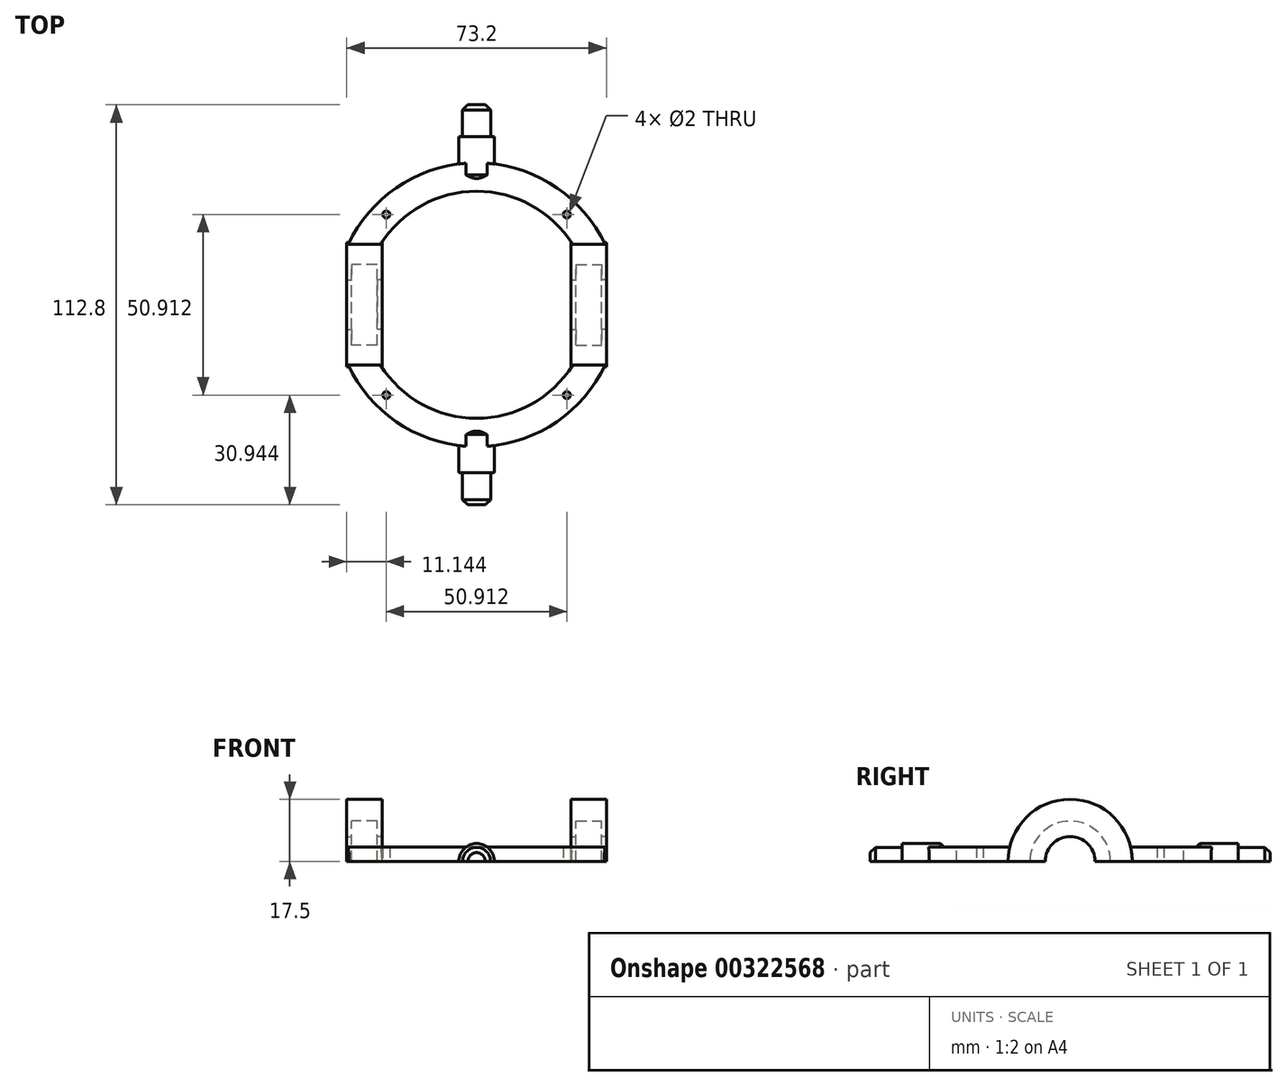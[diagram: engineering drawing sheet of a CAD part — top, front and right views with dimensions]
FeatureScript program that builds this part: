
annotation { "Feature Type Name" : "Feature", "Feature Type Description" : "" }
export const myFeature = defineFeature(function(context is Context, id is Id, definition is map)
    precondition{}
    {
        {
            var Q0;
            Q0=qCreatedBy(makeId("Top.planeOp"),FACE);
            var sketch = newSketch(context, id + "F0", { "sketchPlane" : qUnion([Q0])});
            skCircle(sketch, "E0", {"center": v(0, 0) * mm, "radius": 50 * mm});
            skCircle(sketch, "E1", {"center": v(0, 0) * mm, "radius": 58 * mm});
            skSolve(sketch);
        }
        {
            var Q0;
            Q0=qSketchRegion(id+"F0",true);
            extrude(context, id + "F1", {"entities" : qUnion([Q0]), "depth" : 4 * mm, "hasSecondDirection" : true, "secondDirectionOppositeDirection" : true, "secondDirectionDepth" : 4 * mm});
        }
        {
            var Q0;
            Q0=qCreatedBy(makeId("Front.planeOp"),FACE);
            cPlane(context, id + "F2", {"entities" : qUnion([Q0]), "cplaneType" : CPlaneType.OFFSET, "offset" : 54.8 * mm, "width" : 150 * mm, "height" : 150 * mm});
        }
        {
            var Q0;
            Q0=qCreatedBy(id+"F2.planeOp",FACE);
            var sketch = newSketch(context, id + "F3", { "sketchPlane" : qUnion([Q0])});
            skCircle(sketch, "E2", {"center": v(0, 0) * mm, "radius": 11.35 * mm});
            skCircle(sketch, "E3", {"center": v(0, 0) * mm, "radius": 17.5 * mm});
            skSolve(sketch);
        }
        {
            var Q0;
            Q0=makeQuery(id+"F3.imprint","IMPRINT",FACE,{"disambiguationData":[TD([[makeQuery(id+"F3.imprint","IMPRINT",EDGE,{"derivedFrom":sQuery(id+"F3.wireOp",EDGE,"E2")}),1.0]])]});
            var Q1;
            Q1=makeQuery(id+"F3.imprint","IMPRINT",FACE,{"disambiguationData":[TD([[makeQuery(id+"F3.imprint","IMPRINT",EDGE,{"derivedFrom":sQuery(id+"F3.wireOp",EDGE,"E2")}),-1.0]])]});
            extrude(context, id + "F4", {"entities" : qUnion([Q0, Q1]), "operationType" : NewBodyOperationType.REMOVE, "oppositeDirection" : true, "depth" : 25 * mm, "hasSecondDirection" : true, "secondDirectionOppositeDirection" : false, "secondDirectionDepth" : 25 * mm});
        }
        {
            var Q0;
            Q0=makeQuery(id+"F3.imprint","IMPRINT",FACE,{"disambiguationData":[TD([[makeQuery(id+"F3.imprint","IMPRINT",EDGE,{"derivedFrom":sQuery(id+"F3.wireOp",EDGE,"E2")}),-1.0]])]});
            extrude(context, id + "F5", {"entities" : qUnion([Q0]), "operationType" : NewBodyOperationType.ADD, "oppositeDirection" : true, "depth" : 7.2 * mm});
        }
        {
            var Q0;
            Q0=makeQuery(id+"F5.opExtrude","CAP_FACE",FACE,{"disambiguationData":[OSD([sQuery(id+"F3.wireOp",EDGE,"E2"),sQuery(id+"F3.wireOp",EDGE,"E3")])],"isStart":true});
            var sketch = newSketch(context, id + "F6", { "sketchPlane" : qUnion([Q0])});
            skCircle(sketch, "E4", {"center": v(0, 0) * mm, "radius": 7 * mm});
            skCircle(sketch, "E5", {"center": v(0, 0) * mm, "radius": 17.5 * mm});
            skSolve(sketch);
        }
        {
            var Q0;
            Q0=makeQuery(id+"F6.imprint","IMPRINT",FACE,{"disambiguationData":[TD([[makeQuery(id+"F6.imprint","IMPRINT",EDGE,{"derivedFrom":sQuery(id+"F6.wireOp",EDGE,"E4")}),-1.0]])]});
            var Q1;
            Q1=makeQuery(id+"F6.imprint","IMPRINT",FACE,{"disambiguationData":[TD([[makeQuery(id+"F6.imprint","IMPRINT",EDGE,{"derivedFrom":sQuery(id+"F6.wireOp",EDGE,"E5")}),1.0]])]});
            extrude(context, id + "F7", {"entities" : qUnion([Q0, Q1]), "operationType" : NewBodyOperationType.ADD, "depth" : 1.4 * mm});
        }
        {
            var Q0;
            Q0=makeQuery(id+"F5.opExtrude","CAP_FACE",FACE,{"disambiguationData":[OSD([sQuery(id+"F3.wireOp",EDGE,"E2"),sQuery(id+"F3.wireOp",EDGE,"E3")])],"isStart":false});
            var sketch = newSketch(context, id + "F8", { "sketchPlane" : qUnion([Q0])});
            skCircle(sketch, "E6", {"center": v(0, 0) * mm, "radius": 7 * mm});
            skCircle(sketch, "E7", {"center": v(0, 0) * mm, "radius": 17.5 * mm});
            skSolve(sketch);
        }
        {
            var Q0;
            Q0=makeQuery(id+"F8.imprint","IMPRINT",FACE,{"disambiguationData":[TD([[makeQuery(id+"F8.imprint","IMPRINT",EDGE,{"derivedFrom":sQuery(id+"F8.wireOp",EDGE,"E7")}),-1.0]])]});
            var Q1;
            Q1=makeQuery(id+"F8.imprint","IMPRINT",FACE,{"disambiguationData":[TD([[makeQuery(id+"F8.imprint","IMPRINT",EDGE,{"derivedFrom":sQuery(id+"F8.wireOp",EDGE,"E6")}),-1.0]])]});
            extrude(context, id + "F9", {"entities" : qUnion([Q0, Q1]), "operationType" : NewBodyOperationType.ADD, "depth" : 1.4 * mm});
        }
        {
            var Q0;
            Q0=qCreatedBy(makeId("Front.planeOp"),FACE);
            cPlane(context, id + "F10", {"entities" : qUnion([Q0]), "cplaneType" : CPlaneType.OFFSET, "offset" : 54.8 * mm, "oppositeDirection" : true, "width" : 150 * mm, "height" : 150 * mm});
        }
        {
            var Q0;
            Q0=qCreatedBy(id+"F10.planeOp",FACE);
            var sketch = newSketch(context, id + "F11", { "sketchPlane" : qUnion([Q0])});
            skCircle(sketch, "E8", {"center": v(0, 0) * mm, "radius": 17.5 * mm});
            skCircle(sketch, "E9", {"center": v(0, 0) * mm, "radius": 11.35 * mm});
            skSolve(sketch);
        }
        {
            var Q0;
            Q0=makeQuery(id+"F11.imprint","IMPRINT",FACE,{"disambiguationData":[TD([[makeQuery(id+"F11.imprint","IMPRINT",EDGE,{"derivedFrom":sQuery(id+"F11.wireOp",EDGE,"E8")}),1.0]])]});
            var Q1;
            Q1=makeQuery(id+"F11.imprint","IMPRINT",FACE,{"disambiguationData":[TD([[makeQuery(id+"F11.imprint","IMPRINT",EDGE,{"derivedFrom":sQuery(id+"F11.wireOp",EDGE,"E9")}),1.0]])]});
            extrude(context, id + "F12", {"entities" : qUnion([Q0, Q1]), "operationType" : NewBodyOperationType.REMOVE, "depth" : 25 * mm, "hasSecondDirection" : true, "secondDirectionOppositeDirection" : true, "secondDirectionDepth" : 25 * mm});
        }
        {
            var Q0;
            Q0=makeQuery(id+"F11.imprint","IMPRINT",FACE,{"disambiguationData":[TD([[makeQuery(id+"F11.imprint","IMPRINT",EDGE,{"derivedFrom":sQuery(id+"F11.wireOp",EDGE,"E8")}),1.0]])]});
            extrude(context, id + "F13", {"entities" : qUnion([Q0]), "operationType" : NewBodyOperationType.ADD, "depth" : 7.2 * mm});
        }
        {
            var Q0;
            Q0=makeQuery(id+"F13.opExtrude","CAP_FACE",FACE,{"disambiguationData":[OSD([sQuery(id+"F11.wireOp",EDGE,"E8"),sQuery(id+"F11.wireOp",EDGE,"E9")])],"isStart":true});
            var sketch = newSketch(context, id + "F14", { "sketchPlane" : qUnion([Q0])});
            skCircle(sketch, "E10", {"center": v(0, 0) * mm, "radius": 7 * mm});
            skCircle(sketch, "E11", {"center": v(0, 0) * mm, "radius": 17.5 * mm});
            skSolve(sketch);
        }
        {
            var Q0;
            Q0=makeQuery(id+"F14.imprint","IMPRINT",FACE,{"disambiguationData":[TD([[makeQuery(id+"F14.imprint","IMPRINT",EDGE,{"derivedFrom":makeQuery(id+"F13.opExtrude","CAP_EDGE",EDGE,{"disambiguationData":[OSD([sQuery(id+"F11.wireOp",EDGE,"E9")])],"isStart":true})}),1.0]])]});
            var Q1;
            Q1=makeQuery(id+"F14.imprint","IMPRINT",FACE,{"disambiguationData":[TD([[makeQuery(id+"F14.imprint","IMPRINT",EDGE,{"derivedFrom":sQuery(id+"F14.wireOp",EDGE,"E10")}),-1.0]])]});
            extrude(context, id + "F15", {"entities" : qUnion([Q0, Q1]), "operationType" : NewBodyOperationType.ADD, "depth" : 1.4 * mm});
        }
        {
            var Q0;
            Q0=makeQuery(id+"F13.opExtrude","CAP_FACE",FACE,{"disambiguationData":[OSD([sQuery(id+"F11.wireOp",EDGE,"E8"),sQuery(id+"F11.wireOp",EDGE,"E9")])],"isStart":false});
            var sketch = newSketch(context, id + "F16", { "sketchPlane" : qUnion([Q0])});
            skCircle(sketch, "E12", {"center": v(0, 0) * mm, "radius": 7 * mm});
            skCircle(sketch, "E13", {"center": v(0, 0) * mm, "radius": 17.5 * mm});
            skSolve(sketch);
        }
        {
            var Q0;
            Q0=makeQuery(id+"F16.imprint","IMPRINT",FACE,{"disambiguationData":[TD([[makeQuery(id+"F16.imprint","IMPRINT",EDGE,{"derivedFrom":sQuery(id+"F16.wireOp",EDGE,"E12")}),-1.0]])]});
            var Q1;
            Q1=makeQuery(id+"F16.imprint","IMPRINT",FACE,{"disambiguationData":[TD([[makeQuery(id+"F16.imprint","IMPRINT",EDGE,{"derivedFrom":sQuery(id+"F16.wireOp",EDGE,"E13")}),1.0]])]});
            extrude(context, id + "F17", {"entities" : qUnion([Q0, Q1]), "operationType" : NewBodyOperationType.ADD, "depth" : 1.4 * mm});
        }
        {
            var Q0;
            Q0=makeQuery(id+"F12.boolean.opBoolean","SPLIT",FACE,{"disambiguationData":[OD(0.0)],"derivedFrom":makeQuery(id+"F1.opExtrude","CAP_FACE",FACE,{"disambiguationData":[OSD([sQuery(id+"F0.wireOp",EDGE,"E0"),sQuery(id+"F0.wireOp",EDGE,"E1")])],"isStart":false})});
            var sketch = newSketch(context, id + "F18", { "sketchPlane" : qUnion([Q0])});
            skLineSegment(sketch, "E14", {"start": v(0, 0) * mm, "end": v(-50, 0) * mm, "construction": true});
            skLineSegment(sketch, "E15", {"start": v(-50, 0) * mm, "end": v(-58, 0) * mm, "construction": true});
            skCircle(sketch, "E16", {"center": v(-54, 0) * mm, "radius": 3 * mm});
            skCircle(sketch, "E17", {"center": v(-54, 0) * mm, "radius": 1.5 * mm});
            skCircle(sketch, "E18", {"center": v(-54, 0) * mm, "radius": 1 * mm});
            skCircle(sketch, "E19.1.0", {"center": v(-27, -46.77) * mm, "radius": 3 * mm});
            skCircle(sketch, "E19.1.1", {"center": v(-27, -46.77) * mm, "radius": 1.5 * mm});
            skCircle(sketch, "E19.1.2", {"center": v(-27, -46.77) * mm, "radius": 1 * mm});
            skCircle(sketch, "E19.2.0", {"center": v(27, -46.77) * mm, "radius": 3 * mm});
            skCircle(sketch, "E19.2.1", {"center": v(27, -46.77) * mm, "radius": 1.5 * mm});
            skCircle(sketch, "E19.2.2", {"center": v(27, -46.77) * mm, "radius": 1 * mm});
            skCircle(sketch, "E19.3.0", {"center": v(54, 0) * mm, "radius": 3 * mm});
            skCircle(sketch, "E19.3.1", {"center": v(54, 0) * mm, "radius": 1.5 * mm});
            skCircle(sketch, "E19.3.2", {"center": v(54, 0) * mm, "radius": 1 * mm});
            skCircle(sketch, "E19.4.0", {"center": v(27, 46.77) * mm, "radius": 3 * mm});
            skCircle(sketch, "E19.4.1", {"center": v(27, 46.77) * mm, "radius": 1.5 * mm});
            skCircle(sketch, "E19.4.2", {"center": v(27, 46.77) * mm, "radius": 1 * mm});
            skCircle(sketch, "E19.5.0", {"center": v(-27, 46.77) * mm, "radius": 3 * mm});
            skCircle(sketch, "E19.5.1", {"center": v(-27, 46.77) * mm, "radius": 1.5 * mm});
            skCircle(sketch, "E19.5.2", {"center": v(-27, 46.77) * mm, "radius": 1 * mm});
            skPoint(sketch, "E19.center", {"position": v(0, 0) * mm});
            skSolve(sketch);
        }
        {
            var Q0;
            Q0=makeQuery(id+"F18.imprint","IMPRINT",FACE,{"disambiguationData":[TD([[makeQuery(id+"F18.imprint","IMPRINT",EDGE,{"derivedFrom":sQuery(id+"F18.wireOp",EDGE,"E18")}),1.0]])]});
            var Q1;
            Q1=makeQuery(id+"F18.imprint","IMPRINT",FACE,{"disambiguationData":[TD([[makeQuery(id+"F18.imprint","IMPRINT",EDGE,{"derivedFrom":sQuery(id+"F18.wireOp",EDGE,"E19.5.2")}),1.0]])]});
            var Q2;
            Q2=makeQuery(id+"F18.imprint","IMPRINT",FACE,{"disambiguationData":[TD([[makeQuery(id+"F18.imprint","IMPRINT",EDGE,{"derivedFrom":sQuery(id+"F18.wireOp",EDGE,"E19.4.2")}),1.0]])]});
            var Q3;
            Q3=makeQuery(id+"F18.imprint","IMPRINT",FACE,{"disambiguationData":[TD([[makeQuery(id+"F18.imprint","IMPRINT",EDGE,{"derivedFrom":sQuery(id+"F18.wireOp",EDGE,"E19.3.2")}),1.0]])]});
            var Q4;
            Q4=makeQuery(id+"F18.imprint","IMPRINT",FACE,{"disambiguationData":[TD([[makeQuery(id+"F18.imprint","IMPRINT",EDGE,{"derivedFrom":sQuery(id+"F18.wireOp",EDGE,"E19.2.2")}),1.0]])]});
            var Q5;
            Q5=makeQuery(id+"F18.imprint","IMPRINT",FACE,{"disambiguationData":[TD([[makeQuery(id+"F18.imprint","IMPRINT",EDGE,{"derivedFrom":sQuery(id+"F18.wireOp",EDGE,"E19.1.2")}),1.0]])]});
            extrude(context, id + "F19", {"entities" : qUnion([Q0, Q1, Q2, Q3, Q4, Q5]), "operationType" : NewBodyOperationType.REMOVE, "oppositeDirection" : true, "depth" : 25 * mm});
        }
        {
            var Q0;
            Q0=makeQuery(id+"F18.imprint","IMPRINT",FACE,{"disambiguationData":[TD([[makeQuery(id+"F18.imprint","IMPRINT",EDGE,{"derivedFrom":sQuery(id+"F18.wireOp",EDGE,"E17")}),1.0]])]});
            var Q1;
            Q1=makeQuery(id+"F18.imprint","IMPRINT",FACE,{"disambiguationData":[TD([[makeQuery(id+"F18.imprint","IMPRINT",EDGE,{"derivedFrom":sQuery(id+"F18.wireOp",EDGE,"E19.5.1")}),1.0]])]});
            var Q2;
            Q2=makeQuery(id+"F18.imprint","IMPRINT",FACE,{"disambiguationData":[TD([[makeQuery(id+"F18.imprint","IMPRINT",EDGE,{"derivedFrom":sQuery(id+"F18.wireOp",EDGE,"E19.4.1")}),1.0]])]});
            var Q3;
            Q3=makeQuery(id+"F18.imprint","IMPRINT",FACE,{"disambiguationData":[TD([[makeQuery(id+"F18.imprint","IMPRINT",EDGE,{"derivedFrom":sQuery(id+"F18.wireOp",EDGE,"E19.3.1")}),1.0]])]});
            var Q4;
            Q4=makeQuery(id+"F18.imprint","IMPRINT",FACE,{"disambiguationData":[TD([[makeQuery(id+"F18.imprint","IMPRINT",EDGE,{"derivedFrom":sQuery(id+"F18.wireOp",EDGE,"E19.2.1")}),1.0]])]});
            var Q5;
            Q5=makeQuery(id+"F18.imprint","IMPRINT",FACE,{"disambiguationData":[TD([[makeQuery(id+"F18.imprint","IMPRINT",EDGE,{"derivedFrom":sQuery(id+"F18.wireOp",EDGE,"E19.1.1")}),1.0]])]});
            extrude(context, id + "F20", {"entities" : qUnion([Q0, Q1, Q2, Q3, Q4, Q5]), "operationType" : NewBodyOperationType.REMOVE, "oppositeDirection" : true, "depth" : 4 * mm});
        }
        {
            var Q0;
            Q0=makeQuery(id+"F18.imprint","IMPRINT",FACE,{"disambiguationData":[TD([[makeQuery(id+"F18.imprint","IMPRINT",EDGE,{"derivedFrom":sQuery(id+"F18.wireOp",EDGE,"E16")}),1.0]])]});
            var Q1;
            Q1=makeQuery(id+"F18.imprint","IMPRINT",FACE,{"disambiguationData":[TD([[makeQuery(id+"F18.imprint","IMPRINT",EDGE,{"derivedFrom":sQuery(id+"F18.wireOp",EDGE,"E19.1.0")}),1.0]])]});
            var Q2;
            Q2=makeQuery(id+"F18.imprint","IMPRINT",FACE,{"disambiguationData":[TD([[makeQuery(id+"F18.imprint","IMPRINT",EDGE,{"derivedFrom":sQuery(id+"F18.wireOp",EDGE,"E19.2.0")}),1.0]])]});
            var Q3;
            Q3=makeQuery(id+"F18.imprint","IMPRINT",FACE,{"disambiguationData":[TD([[makeQuery(id+"F18.imprint","IMPRINT",EDGE,{"derivedFrom":sQuery(id+"F18.wireOp",EDGE,"E19.3.0")}),1.0]])]});
            var Q4;
            Q4=makeQuery(id+"F18.imprint","IMPRINT",FACE,{"disambiguationData":[TD([[makeQuery(id+"F18.imprint","IMPRINT",EDGE,{"derivedFrom":sQuery(id+"F18.wireOp",EDGE,"E19.4.0")}),1.0]])]});
            var Q5;
            Q5=makeQuery(id+"F18.imprint","IMPRINT",FACE,{"disambiguationData":[TD([[makeQuery(id+"F18.imprint","IMPRINT",EDGE,{"derivedFrom":sQuery(id+"F18.wireOp",EDGE,"E19.5.0")}),1.0]])]});
            extrude(context, id + "F21", {"entities" : qUnion([Q0, Q1, Q2, Q3, Q4, Q5]), "operationType" : NewBodyOperationType.REMOVE, "oppositeDirection" : true, "depth" : 2 * mm});
        }
        {
            var Q0;
            Q0=qCreatedBy(makeId("Top.planeOp"),FACE);
            var sketch = newSketch(context, id + "F22", { "sketchPlane" : qUnion([Q0])});
            skCircle(sketch, "E20", {"center": v(0, 0) * mm, "radius": 40 * mm});
            skCircle(sketch, "E21", {"center": v(0, 0) * mm, "radius": 32 * mm});
            skSolve(sketch);
        }
        {
            var Q0;
            Q0=qSketchRegion(id+"F22",true);
            extrude(context, id + "F23", {"entities" : qUnion([Q0]), "depth" : 4 * mm, "hasSecondDirection" : true, "secondDirectionOppositeDirection" : true, "secondDirectionDepth" : 4 * mm});
        }
        {
            var Q0;
            Q0=qCreatedBy(makeId("Front.planeOp"),FACE);
            cPlane(context, id + "F24", {"entities" : qUnion([Q0]), "cplaneType" : CPlaneType.OFFSET, "offset" : 35.2 * mm, "width" : 150 * mm, "height" : 150 * mm});
        }
        {
            var Q0;
            Q0=qCreatedBy(id+"F24.planeOp",FACE);
            var sketch = newSketch(context, id + "F25", { "sketchPlane" : qUnion([Q0])});
            skCircle(sketch, "E22.0", {"center": v(0, 0) * mm, "radius": 17.5 * mm});
            skCircle(sketch, "E23.0", {"center": v(0, 0) * mm, "radius": 11.35 * mm});
            skSolve(sketch);
        }
        {
            var Q0;
            Q0=makeQuery(id+"F25.imprint","IMPRINT",FACE,{"disambiguationData":[TD([[makeQuery(id+"F25.imprint","IMPRINT",EDGE,{"derivedFrom":sQuery(id+"F25.wireOp",EDGE,"E22.0")}),1.0]])]});
            var Q1;
            Q1=makeQuery(id+"F25.imprint","IMPRINT",FACE,{"disambiguationData":[TD([[makeQuery(id+"F25.imprint","IMPRINT",EDGE,{"derivedFrom":sQuery(id+"F25.wireOp",EDGE,"E23.0")}),1.0]])]});
            extrude(context, id + "F26", {"entities" : qUnion([Q0, Q1]), "operationType" : NewBodyOperationType.REMOVE, "oppositeDirection" : true, "depth" : 13.4 * mm, "hasSecondDirection" : true, "secondDirectionOppositeDirection" : false, "secondDirectionDepth" : 6.7 * mm});
        }
        {
            var Q0;
            Q0=makeQuery(id+"F25.imprint","IMPRINT",FACE,{"disambiguationData":[TD([[makeQuery(id+"F25.imprint","IMPRINT",EDGE,{"derivedFrom":sQuery(id+"F25.wireOp",EDGE,"E22.0")}),1.0]])]});
            extrude(context, id + "F27", {"entities" : qUnion([Q0]), "operationType" : NewBodyOperationType.ADD, "oppositeDirection" : true, "depth" : 7.2 * mm});
        }
        {
            var Q0;
            Q0=makeQuery(id+"F27.opExtrude","CAP_FACE",FACE,{"disambiguationData":[OSD([sQuery(id+"F25.wireOp",EDGE,"E22.0"),sQuery(id+"F25.wireOp",EDGE,"E23.0")])],"isStart":false});
            var sketch = newSketch(context, id + "F28", { "sketchPlane" : qUnion([Q0])});
            skCircle(sketch, "E24.0", {"center": v(0, 0) * mm, "radius": 7 * mm});
            skCircle(sketch, "E24.1", {"center": v(0, 0) * mm, "radius": 17.5 * mm});
            skSolve(sketch);
        }
        {
            var Q0;
            Q0=makeQuery(id+"F28.imprint","IMPRINT",FACE,{"disambiguationData":[TD([[makeQuery(id+"F28.imprint","IMPRINT",EDGE,{"derivedFrom":makeQuery(id+"F27.opExtrude","CAP_EDGE",EDGE,{"disambiguationData":[OSD([sQuery(id+"F25.wireOp",EDGE,"E23.0")])],"isStart":false})}),1.0]])]});
            var Q1;
            Q1=makeQuery(id+"F28.imprint","IMPRINT",FACE,{"disambiguationData":[TD([[makeQuery(id+"F28.imprint","IMPRINT",EDGE,{"derivedFrom":sQuery(id+"F28.wireOp",EDGE,"E24.0")}),-1.0]])]});
            extrude(context, id + "F29", {"entities" : qUnion([Q0, Q1]), "operationType" : NewBodyOperationType.ADD, "depth" : 1.4 * mm});
        }
        {
            var Q0;
            Q0=makeQuery(id+"F27.opExtrude","CAP_FACE",FACE,{"disambiguationData":[OSD([sQuery(id+"F25.wireOp",EDGE,"E22.0"),sQuery(id+"F25.wireOp",EDGE,"E23.0")])],"isStart":true});
            var sketch = newSketch(context, id + "F30", { "sketchPlane" : qUnion([Q0])});
            skCircle(sketch, "E25.0", {"center": v(0, 0) * mm, "radius": 7 * mm});
            skCircle(sketch, "E25.1", {"center": v(0, 0) * mm, "radius": 17.5 * mm});
            skSolve(sketch);
        }
        {
            var Q0;
            Q0=makeQuery(id+"F30.imprint","IMPRINT",FACE,{"disambiguationData":[TD([[makeQuery(id+"F30.imprint","IMPRINT",EDGE,{"derivedFrom":sQuery(id+"F30.wireOp",EDGE,"E25.1")}),1.0]])]});
            var Q1;
            Q1=makeQuery(id+"F30.imprint","IMPRINT",FACE,{"disambiguationData":[TD([[makeQuery(id+"F30.imprint","IMPRINT",EDGE,{"derivedFrom":sQuery(id+"F30.wireOp",EDGE,"E25.0")}),-1.0]])]});
            extrude(context, id + "F31", {"entities" : qUnion([Q0, Q1]), "operationType" : NewBodyOperationType.ADD, "depth" : 1.4 * mm});
        }
        {
            var Q0;
            Q0=qCreatedBy(makeId("Front.planeOp"),FACE);
            cPlane(context, id + "F32", {"entities" : qUnion([Q0]), "cplaneType" : CPlaneType.OFFSET, "offset" : 35.2 * mm, "oppositeDirection" : true, "width" : 150 * mm, "height" : 150 * mm});
        }
        {
            var Q0;
            Q0=qCreatedBy(id+"F32.planeOp",FACE);
            var sketch = newSketch(context, id + "F33", { "sketchPlane" : qUnion([Q0])});
            skCircle(sketch, "E26.0", {"center": v(0, 0) * mm, "radius": 17.5 * mm});
            skCircle(sketch, "E26.1", {"center": v(0, 0) * mm, "radius": 11.35 * mm});
            skSolve(sketch);
        }
        {
            var Q0;
            Q0=makeQuery(id+"F33.imprint","IMPRINT",FACE,{"disambiguationData":[TD([[makeQuery(id+"F33.imprint","IMPRINT",EDGE,{"derivedFrom":sQuery(id+"F33.wireOp",EDGE,"E26.0")}),1.0]])]});
            var Q1;
            Q1=makeQuery(id+"F33.imprint","IMPRINT",FACE,{"disambiguationData":[TD([[makeQuery(id+"F33.imprint","IMPRINT",EDGE,{"derivedFrom":sQuery(id+"F33.wireOp",EDGE,"E26.1")}),1.0]])]});
            extrude(context, id + "F34", {"entities" : qUnion([Q0, Q1]), "operationType" : NewBodyOperationType.REMOVE, "oppositeDirection" : true, "depth" : 7.2 * mm, "hasSecondDirection" : true, "secondDirectionOppositeDirection" : false, "secondDirectionDepth" : 25 * mm});
        }
        {
            var Q0;
            Q0=makeQuery(id+"F33.imprint","IMPRINT",FACE,{"disambiguationData":[TD([[makeQuery(id+"F33.imprint","IMPRINT",EDGE,{"derivedFrom":sQuery(id+"F33.wireOp",EDGE,"E26.0")}),1.0]])]});
            extrude(context, id + "F35", {"entities" : qUnion([Q0]), "operationType" : NewBodyOperationType.ADD, "depth" : 7.2 * mm});
        }
        {
            var Q0;
            Q0=qCreatedBy(id+"F32.planeOp",FACE);
            var sketch = newSketch(context, id + "F36", { "sketchPlane" : qUnion([Q0])});
            skCircle(sketch, "E27.0", {"center": v(0, 0) * mm, "radius": 7 * mm});
            skCircle(sketch, "E27.1", {"center": v(0, 0) * mm, "radius": 17.5 * mm});
            skSolve(sketch);
        }
        {
            var Q0;
            Q0=makeQuery(id+"F36.imprint","IMPRINT",FACE,{"disambiguationData":[TD([[makeQuery(id+"F36.imprint","IMPRINT",EDGE,{"derivedFrom":sQuery(id+"F36.wireOp",EDGE,"E27.0")}),-1.0]])]});
            extrude(context, id + "F37", {"entities" : qUnion([Q0]), "operationType" : NewBodyOperationType.ADD, "oppositeDirection" : true, "depth" : 1.4 * mm});
        }
        {
            var Q0;
            Q0=makeQuery(id+"F35.opExtrude","CAP_FACE",FACE,{"disambiguationData":[OSD([sQuery(id+"F33.wireOp",EDGE,"E26.0"),sQuery(id+"F33.wireOp",EDGE,"E26.1")])],"isStart":false});
            var sketch = newSketch(context, id + "F38", { "sketchPlane" : qUnion([Q0])});
            skCircle(sketch, "E28.0", {"center": v(0, 0) * mm, "radius": 7 * mm});
            skCircle(sketch, "E28.1", {"center": v(0, 0) * mm, "radius": 17.5 * mm});
            skSolve(sketch);
        }
        {
            var Q0;
            Q0=makeQuery(id+"F38.imprint","IMPRINT",FACE,{"disambiguationData":[TD([[makeQuery(id+"F38.imprint","IMPRINT",EDGE,{"derivedFrom":sQuery(id+"F38.wireOp",EDGE,"E28.0")}),-1.0]])]});
            var Q1;
            Q1=makeQuery(id+"F38.imprint","IMPRINT",FACE,{"disambiguationData":[TD([[makeQuery(id+"F38.imprint","IMPRINT",EDGE,{"derivedFrom":makeQuery(id+"F35.opExtrude","CAP_EDGE",EDGE,{"disambiguationData":[OSD([sQuery(id+"F33.wireOp",EDGE,"E26.1")])],"isStart":false})}),-1.0]])]});
            extrude(context, id + "F39", {"entities" : qUnion([Q0, Q1]), "operationType" : NewBodyOperationType.ADD, "depth" : 1.4 * mm});
        }
        {
            var Q0;
            Q0=qCreatedBy(makeId("Front.planeOp"),FACE);
            var sketch = newSketch(context, id + "F40", { "sketchPlane" : qUnion([Q0])});
            skLineSegment(sketch, "E29", {"start": v(0, 0) * mm, "end": v(0, 51.05) * mm});
            skSolve(sketch);
        }
        {
            var Q0;
            Q0=makeQuery(id+"F23.opExtrude","SWEPT_BODY",BODY,{"disambiguationData":[OSD([sQuery(id+"F22.wireOp",EDGE,"E20"),sQuery(id+"F22.wireOp",EDGE,"E21")])]});
            var Q1;
            Q1=sQuery(id+"F40.wireOp",EDGE,"E29");
            transform(context, id + "F41", {"entities" : qUnion([Q0]), "transformType" : TransformType.ROTATION, "transformAxis" : qUnion([Q1]), "angle" : 90 * degree, "makeCopy" : false});
        }
        {
            var Q0;
            Q0=makeQuery(id+"F17.opExtrude","CAP_FACE",FACE,{"disambiguationData":[OSD([sQuery(id+"F16.wireOp",EDGE,"E12"),sQuery(id+"F16.wireOp",EDGE,"E13")])],"isStart":true});
            var sketch = newSketch(context, id + "F42", { "sketchPlane" : qUnion([Q0])});
            skCircle(sketch, "E30", {"center": v(0, 0) * mm, "radius": 5 * mm});
            skSolve(sketch);
        }
        {
            var Q0;
            Q0=qSketchRegion(id+"F42",true);
            extrude(context, id + "F43", {"entities" : qUnion([Q0]), "operationType" : NewBodyOperationType.ADD, "oppositeDirection" : true, "depth" : 12 * mm, "hasSecondDirection" : true, "secondDirectionOppositeDirection" : false, "secondDirectionDepth" : -.2 * mm});
        }
        {
            var Q0;
            {var subQ0=sQuery(id+"F42.wireOp",EDGE,"E30");Q0=makeQuery(id+"F43.boolean.opBoolean","SPLIT",EDGE,{"disambiguationData":[TD([makeQuery(id+"F23.opExtrude","CAP_FACE",FACE,{"disambiguationData":[OSD([sQuery(id+"F22.wireOp",EDGE,"E20"),sQuery(id+"F22.wireOp",EDGE,"E21")])],"isStart":false})])],"derivedFrom":makeQuery(id+"F43.opExtrude","CAP_EDGE",EDGE,{"disambiguationData":[OSD([subQ0])],"isStart":false})});}
            var Q1;
            {var subQ0=sQuery(id+"F42.wireOp",EDGE,"E30");Q1=makeQuery(id+"F43.boolean.opBoolean","SPLIT",EDGE,{"disambiguationData":[TD([makeQuery(id+"F23.opExtrude","CAP_FACE",FACE,{"disambiguationData":[OSD([sQuery(id+"F22.wireOp",EDGE,"E20"),sQuery(id+"F22.wireOp",EDGE,"E21")])],"isStart":true})])],"derivedFrom":makeQuery(id+"F43.opExtrude","CAP_EDGE",EDGE,{"disambiguationData":[OSD([subQ0])],"isStart":false})});}
            chamfer(context, id + "F44", {"entities" : qUnion([Q0, Q1]), "width" : 1 * mm, "tangentPropagation" : true});
        }
        {
            var Q0;
            Q0=makeQuery(id+"F43.opExtrude","CAP_FACE",FACE,{"disambiguationData":[OSD([sQuery(id+"F42.wireOp",EDGE,"E30")])],"isStart":true});
            var sketch = newSketch(context, id + "F45", { "sketchPlane" : qUnion([Q0])});
            skCircle(sketch, "E31", {"center": v(0, 0) * mm, "radius": 3.95 * mm});
            skSolve(sketch);
        }
        {
            var Q0;
            Q0=makeQuery(id+"F45.imprint","IMPRINT",FACE,{"disambiguationData":[TD([[makeQuery(id+"F45.imprint","IMPRINT",EDGE,{"derivedFrom":sQuery(id+"F45.wireOp",EDGE,"E31")}),1.0]])]});
            extrude(context, id + "F46", {"entities" : qUnion([Q0]), "operationType" : NewBodyOperationType.ADD, "depth" : 9 * mm});
        }
        {
            var Q0;
            Q0=makeQuery(id+"F9.opExtrude","CAP_FACE",FACE,{"disambiguationData":[OSD([sQuery(id+"F8.wireOp",EDGE,"E6"),sQuery(id+"F8.wireOp",EDGE,"E7")])],"isStart":true});
            var sketch = newSketch(context, id + "F47", { "sketchPlane" : qUnion([Q0])});
            skCircle(sketch, "E32", {"center": v(0, 0) * mm, "radius": 5 * mm});
            skSolve(sketch);
        }
        {
            var Q0;
            Q0=qSketchRegion(id+"F47",true);
            extrude(context, id + "F48", {"entities" : qUnion([Q0]), "operationType" : NewBodyOperationType.ADD, "oppositeDirection" : true, "depth" : 12 * mm, "hasSecondDirection" : true, "secondDirectionOppositeDirection" : false, "secondDirectionDepth" : -.2 * mm});
        }
        {
            var Q0;
            {var subQ0=sQuery(id+"F47.wireOp",EDGE,"E32");Q0=makeQuery(id+"F48.boolean.opBoolean","SPLIT",EDGE,{"disambiguationData":[TD([makeQuery(id+"F23.opExtrude","CAP_FACE",FACE,{"disambiguationData":[OSD([sQuery(id+"F22.wireOp",EDGE,"E20"),sQuery(id+"F22.wireOp",EDGE,"E21")])],"isStart":false})])],"derivedFrom":makeQuery(id+"F48.opExtrude","CAP_EDGE",EDGE,{"disambiguationData":[OSD([subQ0])],"isStart":false})});}
            var Q1;
            {var subQ0=sQuery(id+"F47.wireOp",EDGE,"E32");Q1=makeQuery(id+"F48.boolean.opBoolean","SPLIT",EDGE,{"disambiguationData":[TD([makeQuery(id+"F23.opExtrude","CAP_FACE",FACE,{"disambiguationData":[OSD([sQuery(id+"F22.wireOp",EDGE,"E20"),sQuery(id+"F22.wireOp",EDGE,"E21")])],"isStart":true})])],"derivedFrom":makeQuery(id+"F48.opExtrude","CAP_EDGE",EDGE,{"disambiguationData":[OSD([subQ0])],"isStart":false})});}
            chamfer(context, id + "F49", {"entities" : qUnion([Q0, Q1]), "width" : 1 * mm, "tangentPropagation" : true});
        }
        {
            var Q0;
            Q0=makeQuery(id+"F48.opExtrude","CAP_FACE",FACE,{"disambiguationData":[OSD([sQuery(id+"F47.wireOp",EDGE,"E32")])],"isStart":true});
            var sketch = newSketch(context, id + "F50", { "sketchPlane" : qUnion([Q0])});
            skCircle(sketch, "E33", {"center": v(0, 0) * mm, "radius": 3.95 * mm});
            skSolve(sketch);
        }
        {
            var Q0;
            Q0=qSketchRegion(id+"F50",true);
            extrude(context, id + "F51", {"entities" : qUnion([Q0]), "operationType" : NewBodyOperationType.ADD, "depth" : 9 * mm});
        }
        {
            var Q0;
            Q0=makeQuery(id+"F51.opExtrude","CAP_EDGE",EDGE,{"disambiguationData":[OSD([sQuery(id+"F50.wireOp",EDGE,"E33")])],"isStart":false});
            var Q1;
            Q1=makeQuery(id+"F46.opExtrude","CAP_EDGE",EDGE,{"disambiguationData":[OSD([sQuery(id+"F45.wireOp",EDGE,"E31")])],"isStart":false});
            chamfer(context, id + "F52", {"entities" : qUnion([Q0, Q1]), "width" : 1.5 * mm, "tangentPropagation" : true});
        }
        {
            var Q0;
            Q0=makeQuery(id+"F1.opExtrude","SWEPT_BODY",BODY,{"disambiguationData":[OSD([sQuery(id+"F0.wireOp",EDGE,"E0"),sQuery(id+"F0.wireOp",EDGE,"E1")])]});
            deleteBodies(context, id + "F53", {"entities" : qUnion([Q0])});
        }
        {
            var Q0;
            Q0=makeQuery(id+"F34.boolean.opBoolean","SPLIT",FACE,{"disambiguationData":[OD(1.0)],"derivedFrom":makeQuery(id+"F23.opExtrude","CAP_FACE",FACE,{"disambiguationData":[OSD([sQuery(id+"F22.wireOp",EDGE,"E20"),sQuery(id+"F22.wireOp",EDGE,"E21")])],"isStart":false})});
            var sketch = newSketch(context, id + "F54", { "sketchPlane" : qUnion([Q0])});
            skLineSegment(sketch, "E34", {"start": v(0, 0) * mm, "end": v(-25.46, 25.46) * mm, "construction": true});
            skCircle(sketch, "E35", {"center": v(-25.46, 25.46) * mm, "radius": 3 * mm});
            skCircle(sketch, "E36", {"center": v(-25.46, 25.46) * mm, "radius": 1.5 * mm});
            skCircle(sketch, "E37", {"center": v(-25.46, 25.46) * mm, "radius": 1 * mm});
            skCircle(sketch, "E38.1.0", {"center": v(-25.46, -25.46) * mm, "radius": 3 * mm});
            skCircle(sketch, "E38.1.1", {"center": v(-25.46, -25.46) * mm, "radius": 1.5 * mm});
            skCircle(sketch, "E38.1.2", {"center": v(-25.46, -25.46) * mm, "radius": 1 * mm});
            skCircle(sketch, "E38.2.0", {"center": v(25.46, -25.46) * mm, "radius": 3 * mm});
            skCircle(sketch, "E38.2.1", {"center": v(25.46, -25.46) * mm, "radius": 1.5 * mm});
            skCircle(sketch, "E38.2.2", {"center": v(25.46, -25.46) * mm, "radius": 1 * mm});
            skCircle(sketch, "E38.3.0", {"center": v(25.46, 25.46) * mm, "radius": 3 * mm});
            skCircle(sketch, "E38.3.1", {"center": v(25.46, 25.46) * mm, "radius": 1.5 * mm});
            skCircle(sketch, "E38.3.2", {"center": v(25.46, 25.46) * mm, "radius": 1 * mm});
            skPoint(sketch, "E38.center", {"position": v(0, 0) * mm});
            skSolve(sketch);
        }
        {
            var Q0;
            Q0=makeQuery(id+"F54.imprint","IMPRINT",FACE,{"disambiguationData":[TD([[makeQuery(id+"F54.imprint","IMPRINT",EDGE,{"derivedFrom":sQuery(id+"F54.wireOp",EDGE,"E37")}),1.0]])]});
            var Q1;
            Q1=makeQuery(id+"F54.imprint","IMPRINT",FACE,{"disambiguationData":[TD([[makeQuery(id+"F54.imprint","IMPRINT",EDGE,{"derivedFrom":sQuery(id+"F54.wireOp",EDGE,"E38.3.2")}),1.0]])]});
            var Q2;
            Q2=makeQuery(id+"F54.imprint","IMPRINT",FACE,{"disambiguationData":[TD([[makeQuery(id+"F54.imprint","IMPRINT",EDGE,{"derivedFrom":sQuery(id+"F54.wireOp",EDGE,"E38.2.2")}),1.0]])]});
            var Q3;
            Q3=makeQuery(id+"F54.imprint","IMPRINT",FACE,{"disambiguationData":[TD([[makeQuery(id+"F54.imprint","IMPRINT",EDGE,{"derivedFrom":sQuery(id+"F54.wireOp",EDGE,"E38.1.2")}),1.0]])]});
            extrude(context, id + "F55", {"entities" : qUnion([Q0, Q1, Q2, Q3]), "operationType" : NewBodyOperationType.REMOVE, "oppositeDirection" : true, "depth" : 25 * mm});
        }
        {
            var Q0;
            Q0=makeQuery(id+"F54.imprint","IMPRINT",FACE,{"disambiguationData":[TD([[makeQuery(id+"F54.imprint","IMPRINT",EDGE,{"derivedFrom":sQuery(id+"F54.wireOp",EDGE,"E36")}),1.0]])]});
            var Q1;
            Q1=makeQuery(id+"F54.imprint","IMPRINT",FACE,{"disambiguationData":[TD([[makeQuery(id+"F54.imprint","IMPRINT",EDGE,{"derivedFrom":sQuery(id+"F54.wireOp",EDGE,"E38.3.1")}),1.0]])]});
            var Q2;
            Q2=makeQuery(id+"F54.imprint","IMPRINT",FACE,{"disambiguationData":[TD([[makeQuery(id+"F54.imprint","IMPRINT",EDGE,{"derivedFrom":sQuery(id+"F54.wireOp",EDGE,"E38.2.1")}),1.0]])]});
            var Q3;
            Q3=makeQuery(id+"F54.imprint","IMPRINT",FACE,{"disambiguationData":[TD([[makeQuery(id+"F54.imprint","IMPRINT",EDGE,{"derivedFrom":sQuery(id+"F54.wireOp",EDGE,"E38.1.1")}),1.0]])]});
            extrude(context, id + "F56", {"entities" : qUnion([Q0, Q1, Q2, Q3]), "operationType" : NewBodyOperationType.REMOVE, "oppositeDirection" : true, "depth" : 4 * mm});
        }
        {
            var Q0;
            Q0=makeQuery(id+"F54.imprint","IMPRINT",FACE,{"disambiguationData":[TD([[makeQuery(id+"F54.imprint","IMPRINT",EDGE,{"derivedFrom":sQuery(id+"F54.wireOp",EDGE,"E35")}),1.0]])]});
            var Q1;
            Q1=makeQuery(id+"F54.imprint","IMPRINT",FACE,{"disambiguationData":[TD([[makeQuery(id+"F54.imprint","IMPRINT",EDGE,{"derivedFrom":sQuery(id+"F54.wireOp",EDGE,"E38.3.0")}),1.0]])]});
            var Q2;
            Q2=makeQuery(id+"F54.imprint","IMPRINT",FACE,{"disambiguationData":[TD([[makeQuery(id+"F54.imprint","IMPRINT",EDGE,{"derivedFrom":sQuery(id+"F54.wireOp",EDGE,"E38.2.0")}),1.0]])]});
            var Q3;
            Q3=makeQuery(id+"F54.imprint","IMPRINT",FACE,{"disambiguationData":[TD([[makeQuery(id+"F54.imprint","IMPRINT",EDGE,{"derivedFrom":sQuery(id+"F54.wireOp",EDGE,"E38.1.0")}),1.0]])]});
            extrude(context, id + "F57", {"entities" : qUnion([Q0, Q1, Q2, Q3]), "operationType" : NewBodyOperationType.REMOVE, "oppositeDirection" : true, "depth" : 2 * mm});
        }
        {
            var Q0;
            Q0=qCreatedBy(makeId("Top.planeOp"),FACE);
            var sketch = newSketch(context, id + "F58", { "sketchPlane" : qUnion([Q0])});
            skCircle(sketch, "E39", {"center": v(0, 0) * mm, "radius": 76.2 * mm});
            skSolve(sketch);
        }
        {
            var Q0;
            Q0 = qSketchRegion(id + "F58", true);
            extrude(context, id + "F59", {"entities" : qUnion([Q0]), "operationType" : NewBodyOperationType.REMOVE, "depth" : 25 * mm});
        }
        {
            var Q0;
            Q0=qCreatedBy(makeId("Top.planeOp"),FACE);
            var sketch = newSketch(context, id + "F60", { "sketchPlane" : qUnion([Q0])});
            skLineSegment(sketch, "E40", {"start": v(0, 0) * mm, "end": v(0, 13.15) * mm, "construction": true});
            skSolve(sketch);
        }
        {
            var Q0;
            Q0=makeQuery(id+"F23.opExtrude","SWEPT_BODY",BODY,{"disambiguationData":[OSD([sQuery(id+"F22.wireOp",EDGE,"E20"),sQuery(id+"F22.wireOp",EDGE,"E21")])]});
            var Q1;
            Q1=sQuery(id+"F60.wireOp",EDGE,"E40");
            transform(context, id + "F61", {"entities" : qUnion([Q0]), "transformType" : TransformType.ROTATION, "transformAxis" : qUnion([Q1]), "angle" : 180 * degree, "makeCopy" : false});
        }
    });
